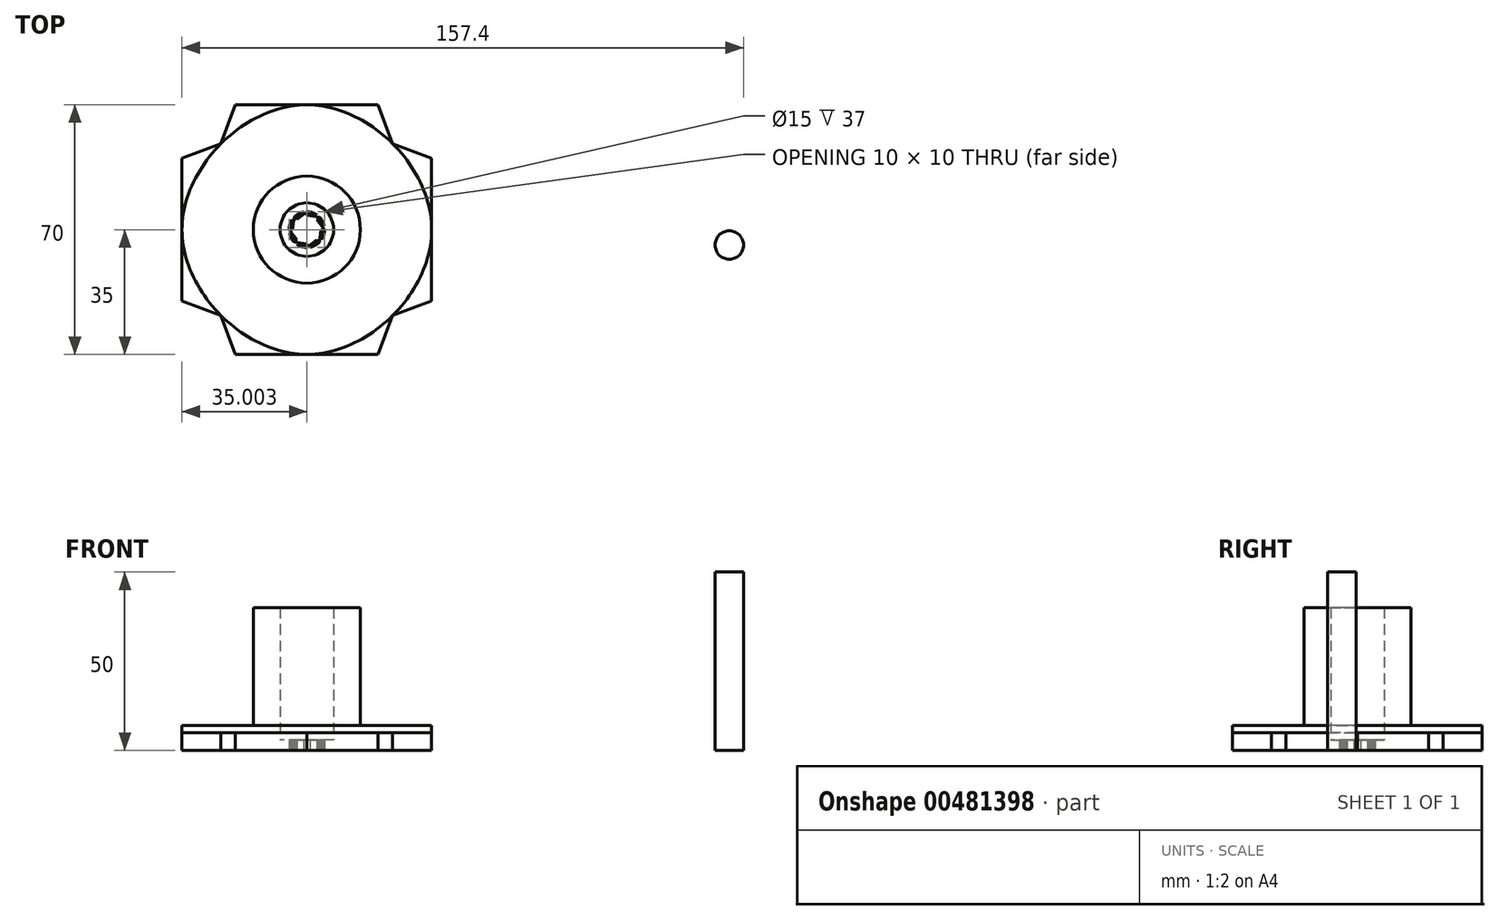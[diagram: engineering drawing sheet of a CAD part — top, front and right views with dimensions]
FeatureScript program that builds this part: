
annotation { "Feature Type Name" : "Feature", "Feature Type Description" : "" }
export const myFeature = defineFeature(function(context is Context, id is Id, definition is map)
    precondition{}
    {
        {
            var Q0;
            Q0=qCreatedBy(makeId("Top.planeOp"),FACE);
            var sketch = newSketch(context, id + "F0", { "sketchPlane" : qUnion([Q0])});
            skFitSpline(sketch, "E0", {"points": [v(-24.36, 20.12) * mm, v(10.64, 55.12) * mm, v(45.64, 20.12) * mm, v(10.64, -14.88) * mm, v(-24.36, 20.12) * mm]});
            skLineSegment(sketch, "E1", {"start": v(-24.36, 40.12) * mm, "end": v(-13.42, 44.18) * mm});
            skLineSegment(sketch, "E2", {"start": v(-13.42, 44.18) * mm, "end": v(-9.36, 55.12) * mm});
            skPoint(sketch, "E3.orphan", {"position": v(-24.36, 55.12) * mm});
            skLineSegment(sketch, "E4", {"start": v(-24.36, 40.12) * mm, "end": v(-24.36, 20.12) * mm});
            skLineSegment(sketch, "E5", {"start": v(-9.36, 55.12) * mm, "end": v(10.64, 55.12) * mm});
            skPoint(sketch, "E6.orphan", {"position": v(45.64, 55.12) * mm});
            skPoint(sketch, "E7.orphan", {"position": v(45.64, -14.88) * mm});
            skPoint(sketch, "E8.left.end.orphan", {"position": v(-24.36, -14.88) * mm});
            skLineSegment(sketch, "E9.MirrorCS", {"start": v(30.64, 55.12) * mm, "end": v(10.64, 55.12) * mm});
            skLineSegment(sketch, "E10.MirrorCS", {"start": v(34.7, 44.18) * mm, "end": v(30.64, 55.12) * mm});
            skLineSegment(sketch, "E11.MirrorCS", {"start": v(45.64, 40.12) * mm, "end": v(34.7, 44.18) * mm});
            skLineSegment(sketch, "E12.MirrorCS", {"start": v(45.64, 40.12) * mm, "end": v(45.64, 20.12) * mm});
            skLineSegment(sketch, "E13.MirrorCS", {"start": v(-24.36, 0.12) * mm, "end": v(-24.36, 20.12) * mm});
            skLineSegment(sketch, "E14.MirrorCS", {"start": v(-24.36, 0.12) * mm, "end": v(-13.42, -3.94) * mm});
            skLineSegment(sketch, "E15.MirrorCS", {"start": v(-13.42, -3.94) * mm, "end": v(-9.36, -14.88) * mm});
            skLineSegment(sketch, "E16.MirrorCS", {"start": v(-9.36, -14.88) * mm, "end": v(10.64, -14.88) * mm});
            skLineSegment(sketch, "E17.MirrorCS", {"start": v(30.64, -14.88) * mm, "end": v(10.64, -14.88) * mm});
            skLineSegment(sketch, "E18.MirrorCS", {"start": v(34.7, -3.94) * mm, "end": v(30.64, -14.88) * mm});
            skLineSegment(sketch, "E19.MirrorCS", {"start": v(45.64, 0.12) * mm, "end": v(45.64, 20.12) * mm});
            skLineSegment(sketch, "E20.MirrorCS", {"start": v(45.64, 0.12) * mm, "end": v(34.7, -3.94) * mm});
            skPoint(sketch, "E21.end.orphan", {"position": v(10.64, 43.08) * mm});
            skPoint(sketch, "E22.end.orphan", {"position": v(0, 20.12) * mm});
            skArc(sketch, "E23", {"start": v(9.72, 25.03) * mm, "mid": v(8.3, 24.54) * mm, "end": v(7.1, 23.66) * mm});
            skCircle(sketch, "E24", {"center": v(10.64, 20.12) * mm, "radius": 7.5 * mm});
            skLineSegment(sketch, "E25", {"start": v(7.46, 23.3) * mm, "end": v(7.81, 22.95) * mm});
            skLineSegment(sketch, "E26", {"start": v(10.64, 24.12) * mm, "end": v(10.64, 24.62) * mm});
            skLineSegment(sketch, "E27", {"start": v(10.64, 24.62) * mm, "end": v(10.64, 24.12) * mm});
            skLineSegment(sketch, "E28", {"start": v(13.83, 23.3) * mm, "end": v(13.47, 22.95) * mm});
            skLineSegment(sketch, "E29", {"start": v(15.14, 20.12) * mm, "end": v(14.64, 20.12) * mm});
            skLineSegment(sketch, "E30", {"start": v(13.83, 16.94) * mm, "end": v(13.47, 17.3) * mm});
            skLineSegment(sketch, "E31", {"start": v(10.64, 15.62) * mm, "end": v(10.64, 16.12) * mm});
            skLineSegment(sketch, "E32", {"start": v(7.46, 16.94) * mm, "end": v(7.81, 17.3) * mm});
            skLineSegment(sketch, "E33", {"start": v(7.81, 17.3) * mm, "end": v(5.64, 20.12) * mm});
            skLineSegment(sketch, "E34", {"start": v(7.81, 22.95) * mm, "end": v(10.64, 25.12) * mm});
            skLineSegment(sketch, "E35", {"start": v(10.64, 24.12) * mm, "end": v(14.18, 23.66) * mm});
            skLineSegment(sketch, "E36", {"start": v(13.47, 22.95) * mm, "end": v(15.64, 20.12) * mm});
            skLineSegment(sketch, "E37", {"start": v(14.64, 20.12) * mm, "end": v(14.18, 16.58) * mm});
            skLineSegment(sketch, "E38", {"start": v(13.47, 17.3) * mm, "end": v(10.64, 15.12) * mm});
            skLineSegment(sketch, "E39", {"start": v(10.64, 16.12) * mm, "end": v(7.1, 16.58) * mm});
            skLineSegment(sketch, "E40", {"start": v(7.81, 17.3) * mm, "end": v(7.46, 16.94) * mm});
            skLineSegment(sketch, "E41", {"start": v(7.46, 16.94) * mm, "end": v(5.73, 19.2) * mm});
            skPoint(sketch, "E42.end.orphan", {"position": v(6.64, 20.12) * mm});
            skLineSegment(sketch, "E43", {"start": v(6.64, 20.12) * mm, "end": v(6.14, 20.12) * mm});
            skLineSegment(sketch, "E44", {"start": v(6.14, 20.12) * mm, "end": v(6.64, 20.12) * mm});
            skLineSegment(sketch, "E45", {"start": v(6.64, 20.12) * mm, "end": v(7.1, 23.66) * mm});
            skLineSegment(sketch, "E46", {"start": v(6.14, 20.12) * mm, "end": v(6.51, 22.94) * mm});
            skLineSegment(sketch, "E47", {"start": v(7.46, 23.3) * mm, "end": v(9.72, 25.03) * mm});
            skLineSegment(sketch, "E48", {"start": v(10.64, 24.62) * mm, "end": v(13.46, 24.25) * mm});
            skLineSegment(sketch, "E49", {"start": v(13.83, 23.3) * mm, "end": v(15.56, 21.05) * mm});
            skLineSegment(sketch, "E50", {"start": v(15.14, 20.12) * mm, "end": v(14.77, 17.3) * mm});
            skLineSegment(sketch, "E51", {"start": v(13.83, 16.94) * mm, "end": v(11.57, 15.2) * mm});
            skLineSegment(sketch, "E52", {"start": v(10.64, 15.62) * mm, "end": v(7.82, 16) * mm});
            skLineSegment(sketch, "E53.trimOffspring", {"start": v(7.46, 16.94) * mm, "end": v(7.64, 17.11) * mm});
            skPoint(sketch, "E54.start.orphan", {"position": v(6.88, 21.89) * mm});
            skPoint(sketch, "E55.end.orphan", {"position": v(6.73, 18.7) * mm});
            skPoint(sketch, "E55.start.orphan", {"position": v(7.64, 17.11) * mm});
            skArc(sketch, "E56", {"start": v(6.51, 22.94) * mm, "mid": v(5.87, 21.6) * mm, "end": v(5.64, 20.12) * mm});
            skCircle(sketch, "E57", {"center": v(129.06, 15.79) * mm, "radius": 3.97 * mm});
            skArc(sketch, "E58.trimOffspring", {"start": v(15.56, 21.05) * mm, "mid": v(15.06, 22.46) * mm, "end": v(14.18, 23.66) * mm});
            skArc(sketch, "E59.trimOffspring", {"start": v(14.77, 17.3) * mm, "mid": v(15.42, 18.64) * mm, "end": v(15.64, 20.12) * mm});
            skArc(sketch, "E60.trimOffspring", {"start": v(11.57, 15.2) * mm, "mid": v(12.98, 15.7) * mm, "end": v(14.18, 16.58) * mm});
            skArc(sketch, "E61.trimOffspring", {"start": v(7.82, 16) * mm, "mid": v(9.17, 15.34) * mm, "end": v(10.64, 15.12) * mm});
            skArc(sketch, "E62.trimOffspring", {"start": v(5.73, 19.2) * mm, "mid": v(6.22, 17.78) * mm, "end": v(7.1, 16.58) * mm});
            skCircle(sketch, "E63", {"center": v(10.64, 20.12) * mm, "radius": 15 * mm});
            skArc(sketch, "E64.trimOffspring", {"start": v(13.46, 24.25) * mm, "mid": v(12.12, 24.9) * mm, "end": v(10.64, 25.12) * mm});
            skSolve(sketch);
        }
        {
            var Q0;
            {var subQ0=sQuery(id+"F0.wireOp",EDGE,"E1");Q0=makeQuery(id+"F0.imprint","IMPRINT",FACE,{"disambiguationData":[TD([[makeQuery(id+"F0.imprint","IMPRINT",EDGE,{"derivedFrom":subQ0}),-1.0]])]});}
            var Q1;
            {var subQ0=sQuery(id+"F0.wireOp",EDGE,"E2");Q1=makeQuery(id+"F0.imprint","IMPRINT",FACE,{"disambiguationData":[TD([[makeQuery(id+"F0.imprint","IMPRINT",EDGE,{"derivedFrom":subQ0}),-1.0]])]});}
            var Q2;
            {var subQ0=sQuery(id+"F0.wireOp",EDGE,"E9.MirrorCS");Q2=makeQuery(id+"F0.imprint","IMPRINT",FACE,{"disambiguationData":[TD([[makeQuery(id+"F0.imprint","IMPRINT",EDGE,{"derivedFrom":subQ0}),1.0]])]});}
            var Q3;
            {var subQ0=sQuery(id+"F0.wireOp",EDGE,"E11.MirrorCS");Q3=makeQuery(id+"F0.imprint","IMPRINT",FACE,{"disambiguationData":[TD([[makeQuery(id+"F0.imprint","IMPRINT",EDGE,{"derivedFrom":subQ0}),1.0]])]});}
            var Q4;
            {var subQ0=sQuery(id+"F0.wireOp",EDGE,"E19.MirrorCS");Q4=makeQuery(id+"F0.imprint","IMPRINT",FACE,{"disambiguationData":[TD([[makeQuery(id+"F0.imprint","IMPRINT",EDGE,{"derivedFrom":subQ0}),1.0]])]});}
            var Q5;
            {var subQ0=sQuery(id+"F0.wireOp",EDGE,"E17.MirrorCS");Q5=makeQuery(id+"F0.imprint","IMPRINT",FACE,{"disambiguationData":[TD([[makeQuery(id+"F0.imprint","IMPRINT",EDGE,{"derivedFrom":subQ0}),-1.0]])]});}
            var Q6;
            {var subQ0=sQuery(id+"F0.wireOp",EDGE,"E15.MirrorCS");Q6=makeQuery(id+"F0.imprint","IMPRINT",FACE,{"disambiguationData":[TD([[makeQuery(id+"F0.imprint","IMPRINT",EDGE,{"derivedFrom":subQ0}),1.0]])]});}
            var Q7;
            {var subQ0=sQuery(id+"F0.wireOp",EDGE,"E13.MirrorCS");Q7=makeQuery(id+"F0.imprint","IMPRINT",FACE,{"disambiguationData":[TD([[makeQuery(id+"F0.imprint","IMPRINT",EDGE,{"derivedFrom":subQ0}),-1.0]])]});}
            extrude(context, id + "F1", {"entities" : qUnion([Q0, Q1, Q2, Q3, Q4, Q5, Q6, Q7]), "depth" : 5 * mm, "offsetDistance" : 25 * mm});
        }
        {
            var Q0;
            Q0=makeQuery(id+"F0.imprint","IMPRINT",FACE,{"disambiguationData":[TD([[makeQuery(id+"F0.imprint","IMPRINT",EDGE,{"derivedFrom":sQuery(id+"F0.wireOp",EDGE,"E63")}),-1.0]])]});
            extrude(context, id + "F2", {"entities" : qUnion([Q0]), "depth" : 7 * mm, "offsetDistance" : 25 * mm});
        }
        {
            var Q0;
            Q0=makeQuery(id+"F0.imprint","IMPRINT",FACE,{"disambiguationData":[TD([[makeQuery(id+"F0.imprint","IMPRINT",EDGE,{"derivedFrom":sQuery(id+"F0.wireOp",EDGE,"E24")}),-1.0]])]});
            extrude(context, id + "F3", {"entities" : qUnion([Q0]), "operationType" : NewBodyOperationType.ADD, "depth" : 40 * mm, "offsetDistance" : 25 * mm});
        }
        {
            var Q0;
            Q0=makeQuery(id+"F0.imprint","IMPRINT",FACE,{"disambiguationData":[TD([[makeQuery(id+"F0.imprint","IMPRINT",EDGE,{"derivedFrom":sQuery(id+"F0.wireOp",EDGE,"E24")}),1.0]])]});
            extrude(context, id + "F4", {"entities" : qUnion([Q0]), "operationType" : NewBodyOperationType.ADD, "depth" : 3 * mm, "offsetDistance" : 25 * mm});
        }
        {
            var Q0;
            Q0=makeQuery(id+"F0.imprint","IMPRINT",FACE,{"disambiguationData":[TD([[makeQuery(id+"F0.imprint","IMPRINT",EDGE,{"derivedFrom":sQuery(id+"F0.wireOp",EDGE,"E57")}),1.0]])]});
            extrude(context, id + "F5", {"entities" : qUnion([Q0]), "depth" : 50 * mm, "offsetDistance" : 25 * mm});
        }
    });
